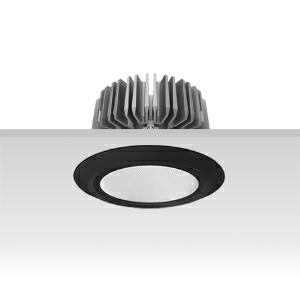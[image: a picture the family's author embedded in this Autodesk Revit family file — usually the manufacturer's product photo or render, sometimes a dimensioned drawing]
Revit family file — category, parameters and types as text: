
# Revit family: 3f_filippi_-_3f_reno_bianco_ampio_3f_filippi_-_30341_a01047_-_3f_reno_150_wh_2000-840_wide___smp_bk_b096
name_source: partatom
category: Lighting Fixtures
units: mm (PartAtom-declared; Revit-internal decimal feet)

## family parameters
Cut with Voids When Loaded = No
Host = Face
Light Source = No
Part Type = Normal
Room Calculation Point = No
Round Connector Dimension = Use Diameter
Shared = No

## types (1)
- 3F Filippi - 3F Reno Bianco Ampio (1 x LED, 1726 lm, 20 W, 4000 K)
    Apparent Load = 20 VA
    Approval mark = CE
    CIE Flux Codes = 73 92 98 100 100
    Color Rendering = 80
    Color Temperature = 4000 K
    Control Gear = Electronic ballast
    Default Elevation = 1800 mm
    Description = ILLUMINOTECHNICAL
Luminous efficiency 100% (DLOR 100%, ULOR 0%).
Initial luminous flux of the luminaire 1726 lm.
Direct symmetric wide distribution.
Installation Interdistance Transv.D = 1.01 x hu - Long.D = 1.00 x hu.
Tabular UGR (CIE 117 - 4H-8H; S=0.25H; 70/50/20): RUG 23.4 - 23.4.
Beam angle: 70° - 70°.
Luminous efficacy 86 lm/W.
Lifetime (L90/B10): 30000 h. (tq+25°C)
Lifetime (L85/B10): 50000 h. (tq+25°C)
Lifetime (L70/B10): 80000 h. (tq+25°C)
Sudden decreased luminous flux after 50000 hours: 0% (C0).
Photobiological safety in compliance with IEC/TR 62778: RG0 risk exempt, (IEC 62471).
In compliance with IEC/EN 62722-2-1 - IEC/EN 62717 standards.

SOURCE
Compact LED module 2000/840.
Energy efficiency class (UE 2019/2020 - UE 2019/2015): D.
CIE 13.3 Colour rendering index: CRI >80 (R9 <50%).
IES TM-30 Fidelity Index: Rf = 84 Rg = 95.
CCT nominal colour temperature 4000 K.
Colour initial tolerance (MacAdam): SDCM 3.
Zhaga Book 3 compliant.

MECHANICAL
Passive heat dissipator in die-casting aluminium, oversized, for optimum thermal management of the LED module.
Parabolic element with graduated/concentric rings in white polycarbonate.
Transparent external lens with glossy and satin differentiated surfaces, with a cooling and anti-insect system in methacrylate (PMMA).
Fastening spring clips in stainless steel.
Dimensions: diameter 176 mm, height 111 mm. Weight 0.74 kg.
IP44 protection degree for exposed part, IP20 for recessed part.
Mechanical strength to impacts IK05 (0.7 joule).
Glow-wire test resistance 650°C.

ELECTRICAL
Wiring on a separate unit.
Halogen Free electronic wiring 230V-50/60Hz, power factor 0.95, THD <25%, constant output current, SELV, class II, 1 driver.
Power of the luminaire 20 W.
ENEC - CE.
SAFE FLICKER: PstLM=<1 and SVM=<0.4 (IEC TR 61547-1 and IEC TR 63158), to ensure a more comfortable and safe light.
Luminaire compliant with EN 60598-2-22 for power supply from a centralised emergency system CPSS (Central Power Supply System), not incorporated in the luminaire - high risk areas excluded. The default power and flux are 100% in AC and 100% in DC.
Ambient temperature from 0°C to +25°C.
Temperature class T6 max 85°C.
Relative humidity UR: <85%.

INSTALLATION
Pull-up recessed fitting.
False ceiling carving: 150 mm.
All accessories dedicated to this product are available on the Catalog and on our website www.3F-Filippi.com.

ACCESSORIES
A01047 - Anti-glare microprismatic SMP diffuser in methacrylate (PMMA), locked and in line with the trim, in black polycarbonate.

APPLICATIONS
Suitable product for food production plants (HACCP), IFS (Food Version 6), BRC (GSFS Food Version 7).
Environments: architectural, commercial, exhibition areas, transit areas, corridors, shops, display windows, service areas.
In false ceilings with narrow voids.

WARNING
Luminaire designed for disposal/recycling at end-of-life.
Replaceable (LED only) light source by a professional. Replaceable control gear by a professional.
    Height = 0 mm  [stored 0 ft]
    Lamp = 1 x LED
    Lamp Light Flux = 1726 lm
    Lamp Power = 20 W
    Lamp count = 1
    Length = 176 mm
    Lifetime = 50000 h
    Luminous efficacy = 86 lm/W
    Manufacturer = 3F Filippi
    ModVariant = No
    Model = 3F Filippi - 30341+A01047 - 3F Reno 150 WH 2000-840 WIDE + SMP BK
    Mounting Place = Ceiling
    Mounting Type = Recessed
    Number of Poles = 1
    OnlyDefault = Yes
    Power Factor = 1
    Product Name = 3F Filippi - 3F Reno Bianco Ampio
    Product group = recessed luminaire
    ProductGroupID = 4
    Protection Class = Protection class II
    Protection Degree = IP 20
    RLX_Detail_Level = 1
    RLX_Emergency_Light_Flux = 0 lm
    RLX_Emergency_Type = 0
    RLX_Emergency_Type_DB = No
    RlxData = <blob elided: 86685 chars, md5=96ce63fc>
    Socket = socket
    Standby Power = 0 W
    System Light Flux = 1726 lm
    System Power = 20 W
    Type Comments = Product without accessories
    Type Image = 3ffilippi_3f_reno_150_bk_vs_smp.jpg
    URL = http://relux.com
    VarID = ---
    Voltage = 0 V
    Weight = 0.00 kg
    Width = 0 mm  [stored 0 ft]

note: [stored X ft] marks values corroborated as IEEE doubles in the binary element streams (Revit-internal decimal feet)

## geometry (parser evidence)
native form markers: Blend x4, Sweep x9
no freeform markers — native parametric forms only
